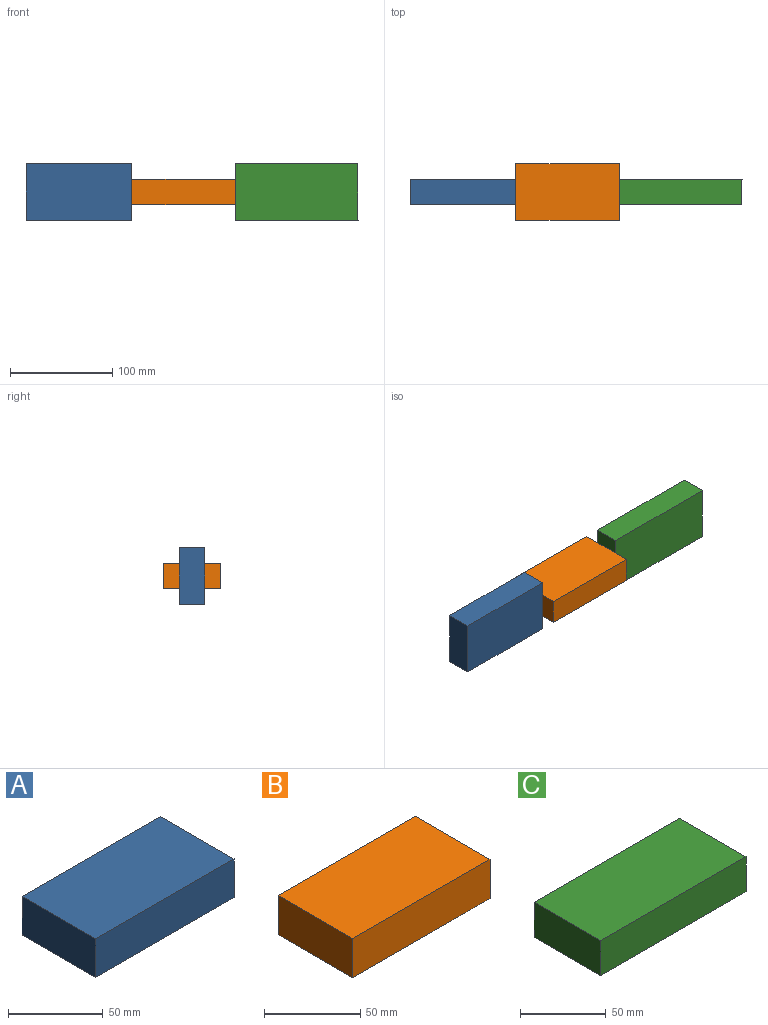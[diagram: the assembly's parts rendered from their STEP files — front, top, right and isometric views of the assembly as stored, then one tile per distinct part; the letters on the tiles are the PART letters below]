
ASSEMBLY  parts=3 mates=2
PART A: 6 faces, bbox 103.5x55x25 mm
  f0: plane 103.5x55mm, normal (0,0,1), area 5692.5mm2, adj f1,f3,f4,f5
  f1: plane 55x25mm, normal (-1,0,0), area 1375mm2, adj f0,f2,f4,f5
  f2: plane 103.5x55mm, normal (0,0,-1), area 5692.5mm2, adj f1,f3,f4,f5
  f3: plane 55x25mm, normal (1,0,0), area 1375mm2, adj f0,f2,f4,f5
  f4: plane 103.5x25mm, normal (0,-1,0), area 2587.5mm2, adj f0,f1,f2,f3
  f5: plane 103.5x25mm, normal (0,1,0), area 2587.5mm2, adj f0,f1,f2,f3
PART B: 6 faces, bbox 101x55x25 mm
  f0: plane 101x55mm, normal (0,0,1), area 5555mm2, adj f1,f3,f4,f5
  f1: plane 55x25mm, normal (-1,0,0), area 1375mm2, adj f0,f2,f4,f5
  f2: plane 101x55mm, normal (0,0,-1), area 5555mm2, adj f1,f3,f4,f5
  f3: plane 55x25mm, normal (1,0,0), area 1375mm2, adj f0,f2,f4,f5
  f4: plane 101x25mm, normal (0,-1,0), area 2525mm2, adj f0,f1,f2,f3
  f5: plane 101x25mm, normal (0,1,0), area 2525mm2, adj f0,f1,f2,f3
PART C: 6 faces, bbox 120x55x25 mm
  f0: plane 120x55mm, normal (0,0,1), area 6600mm2, adj f1,f3,f4,f5
  f1: plane 55x25mm, normal (-1,0,0), area 1375mm2, adj f0,f2,f4,f5
  f2: plane 120x55mm, normal (0,0,-1), area 6600mm2, adj f1,f3,f4,f5
  f3: plane 55x25mm, normal (1,0,0), area 1375mm2, adj f0,f2,f4,f5
  f4: plane 120x25mm, normal (0,-1,0), area 3000mm2, adj f0,f1,f2,f3
  f5: plane 120x25mm, normal (0,1,0), area 3000mm2, adj f0,f1,f2,f3
PLACE A rot(axis=(-1,0,0),90deg) t=(-105.6,66.57,32.88)mm
PLACE B t=(0.37,94.07,60.38)mm
PLACE C rot(axis=(1,0,0),90deg) t=(107.15,66.57,87.88)mm
MATE ball A.f3 <-> B.f1  axis (1,0,0) through (-53.85,66.57,60.38)mm
MATE ball C.f1 <-> B.f3  axis (-1,0,0) through (47.15,66.57,60.38)mm
